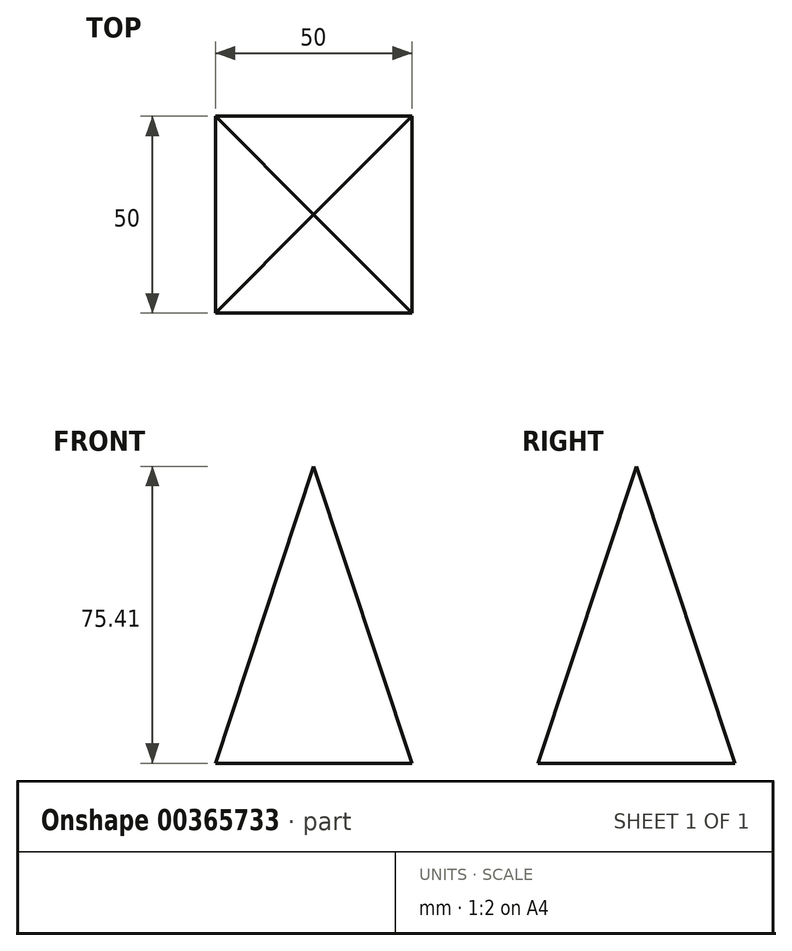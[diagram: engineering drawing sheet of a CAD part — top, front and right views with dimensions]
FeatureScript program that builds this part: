
annotation { "Feature Type Name" : "Feature", "Feature Type Description" : "" }
export const myFeature = defineFeature(function(context is Context, id is Id, definition is map)
    precondition{}
    {
        {
            var Q0;
            Q0=qCreatedBy(makeId("Top.planeOp"),FACE);
            var sketch = newSketch(context, id + "F0", { "sketchPlane" : qUnion([Q0])});
            skLineSegment(sketch, "E0.bottom", {"start": v(25, 25) * mm, "end": v(-25, 25) * mm});
            skLineSegment(sketch, "E0.top", {"start": v(25, -25) * mm, "end": v(-25, -25) * mm});
            skLineSegment(sketch, "E0.left", {"start": v(25, 25) * mm, "end": v(25, -25) * mm});
            skLineSegment(sketch, "E0.right", {"start": v(-25, 25) * mm, "end": v(-25, -25) * mm});
            skPoint(sketch, "E0.middle", {"position": v(0, 0) * mm});
            skSolve(sketch);
        }
        {
            var Q0;
            Q0=qCreatedBy(makeId("Front.planeOp"),FACE);
            var sketch = newSketch(context, id + "F1", { "sketchPlane" : qUnion([Q0])});
            skPoint(sketch, "E1", {"position": v(0, 75.4) * mm});
            skSolve(sketch);
        }
        {
            var Q0;
            Q0=makeQuery(id+"F0.imprint","IMPRINT",FACE,{"disambiguationData":[TD([[makeQuery(id+"F0.imprint","IMPRINT",EDGE,{"derivedFrom":sQuery(id+"F0.wireOp",EDGE,"E0.bottom")}),1.0]])]});
            var Q1;
            Q1=sQuery(id+"F1.wireOp",VERTEX,"E1");
            loft(context, id + "F2", {"sheetProfilesArray" : [{ "sheetProfileEntities" : qUnion([Q0]) }, { "sheetProfileEntities" : qUnion([Q1]) }]});
        }
    });
